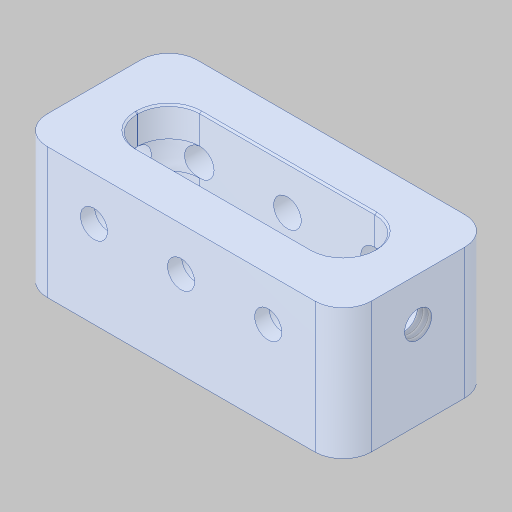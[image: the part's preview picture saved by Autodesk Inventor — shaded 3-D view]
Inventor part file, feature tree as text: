
AUTODESK INVENTOR PART (.ipt)
format: ipt  version: 2023.5 (Build 275446000, 446)  size: 388,096 bytes
history: native  units: in
note: dims shown in document units (in); Inventor stores cm internally (conversion verified against a paired STEP export)
features: sketch x4, hole x3, projected_geometry x2, extrude x1, chamfer x1
ambient origin geometry x8: Origin, YZ Plane, XZ Plane, XY Plane, X Axis, Y Axis, Z Axis, Center Point
bodies: Solid1 (feature_tree)
feature tree (11):
  extrude  "Extrusion1"  Depth=1.0in TaperAngle=0.0deg
  hole  "Hole1"  [1 undecoded]
  hole  "Hole2"  [1 undecoded]
  hole  "Hole3"  [1 undecoded]
  sketch  "Sketch1"  dims[d0=0.0625in d1=1.0in d2=0.0in]
  projected_geometry  "Projected Loop1"
  sketch  "Sketch2"  dims[d3=0.156in d4=0.38in d5=0.385in d6=0.25in d7=0.563in d8=1.0in d9=0.8108in]
  projected_geometry  "Projected Loop2"
  sketch  "Sketch3"  dims[d10=0.151in d11=0.38in d12=0.375in d13=0.25in d14=0.5635in d15=1.0in d16=0.8108in]
  sketch  "Sketch4"  dims[d17=0.156in d18=0.38in d19=0.385in d20=0.25in d21=0.563in d22=1.0in d23=0.8108in d24=1.0in d25=1.0in d26=1.0in d27=0.15in d28=0.25in d29=0.375in d30=32.2835in d31=0.75in d32=46.4567in d33=0.0625in d34=0.75in d35=0.375in]
  chamfer  "Chamfer2"  Distance=0.15in
note: 3 required parameter values undecoded (feature->parameter linkage not recoverable at this tier; creation-order binding heuristic only, values carry confidence <= 0.55)
